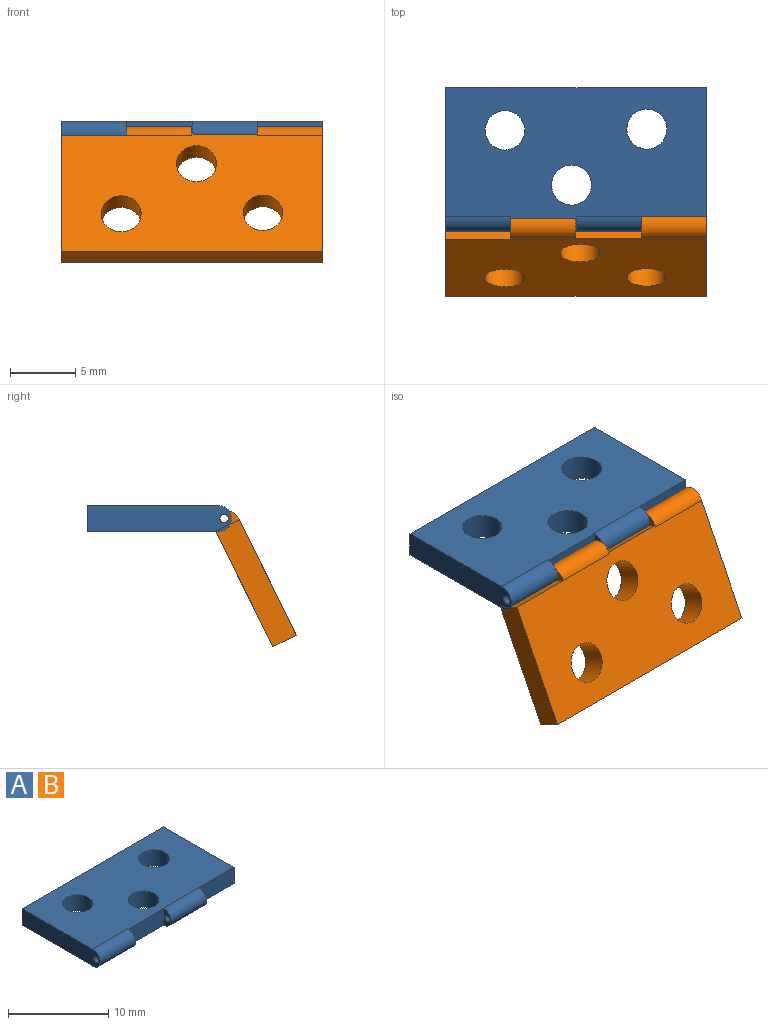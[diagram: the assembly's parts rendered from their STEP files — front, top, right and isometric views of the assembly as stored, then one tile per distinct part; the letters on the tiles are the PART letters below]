
ASSEMBLY  parts=2 mates=1
PART A: 17 faces, bbox 20x11x2 mm
  f0: plane 5x2mm, normal (0,-1,0), area 10mm2, adj f1,f2,f11,f12
  f1: plane 20x10mm, normal (0,0,1), area 176.2mm2, adj f0,f3,f4,f5,f6,f7,f8,f9
  f2: plane 20x10mm, normal (0,0,-1), area 176.2mm2, adj f0,f3,f4,f5,f6,f7,f8,f9
  f3: plane 11.01x2.02mm, normal (-1,0,0), area 21.2mm2, adj f1,f2,f5,f10,f16
  f4: plane 9.88x2mm, normal (1,0,0), area 19.8mm2, adj f1,f2,f5,f13
  f5: plane 20x2mm, normal (0,1,0), area 40mm2, adj f1,f2,f3,f4
  f6: cylinder r=1.53mm len=3.07mm, axis (0,0,1), area 19.3mm2, adj f1,f2
  f7: cylinder r=1.51mm len=3.03mm, axis (0,0,1), area 19mm2, adj f1,f2
  f8: cylinder r=1.53mm len=3.07mm, axis (0,0,1), area 19.3mm2, adj f1,f2
  f9: cylinder r=1.01mm len=5mm, axis (1,0,0), area 17.1mm2, adj f1,f2,f12,f14
  f10: cylinder r=1.01mm len=5mm, axis (-1,0,0), area 17.1mm2, adj f1,f2,f3,f11
  f11: plane 2.02x1.13mm, normal (1,0,0), area 1.2mm2, adj f0,f1,f2,f10,f16
  f12: plane 2.02x1.13mm, normal (-1,0,0), area 1.2mm2, adj f0,f1,f2,f9,f15
  f13: plane 5x2mm, normal (0,-1,0), area 10mm2, adj f1,f2,f4,f14
  f14: plane 2.02x1.13mm, normal (1,0,0), area 1.5mm2, adj f9,f13,f15
  f15: cylinder r=0.33mm len=5mm, axis (-1,0,0), area 10.5mm2, adj f12,f14
  f16: cylinder r=0.33mm len=5mm, axis (-1,0,0), area 10.5mm2, adj f3,f11
PART B: same geometry as A
PLACE A t=(1.73,0.68,4.97)mm fixed
PLACE B rot(axis=(0,0.53,-0.85),180deg) t=(2.43,0.93,5.12)mm
MATE revolute B.f15 <-> A.f15  axis (-1,0,0) through (7.08,0.23,5.97)mm
